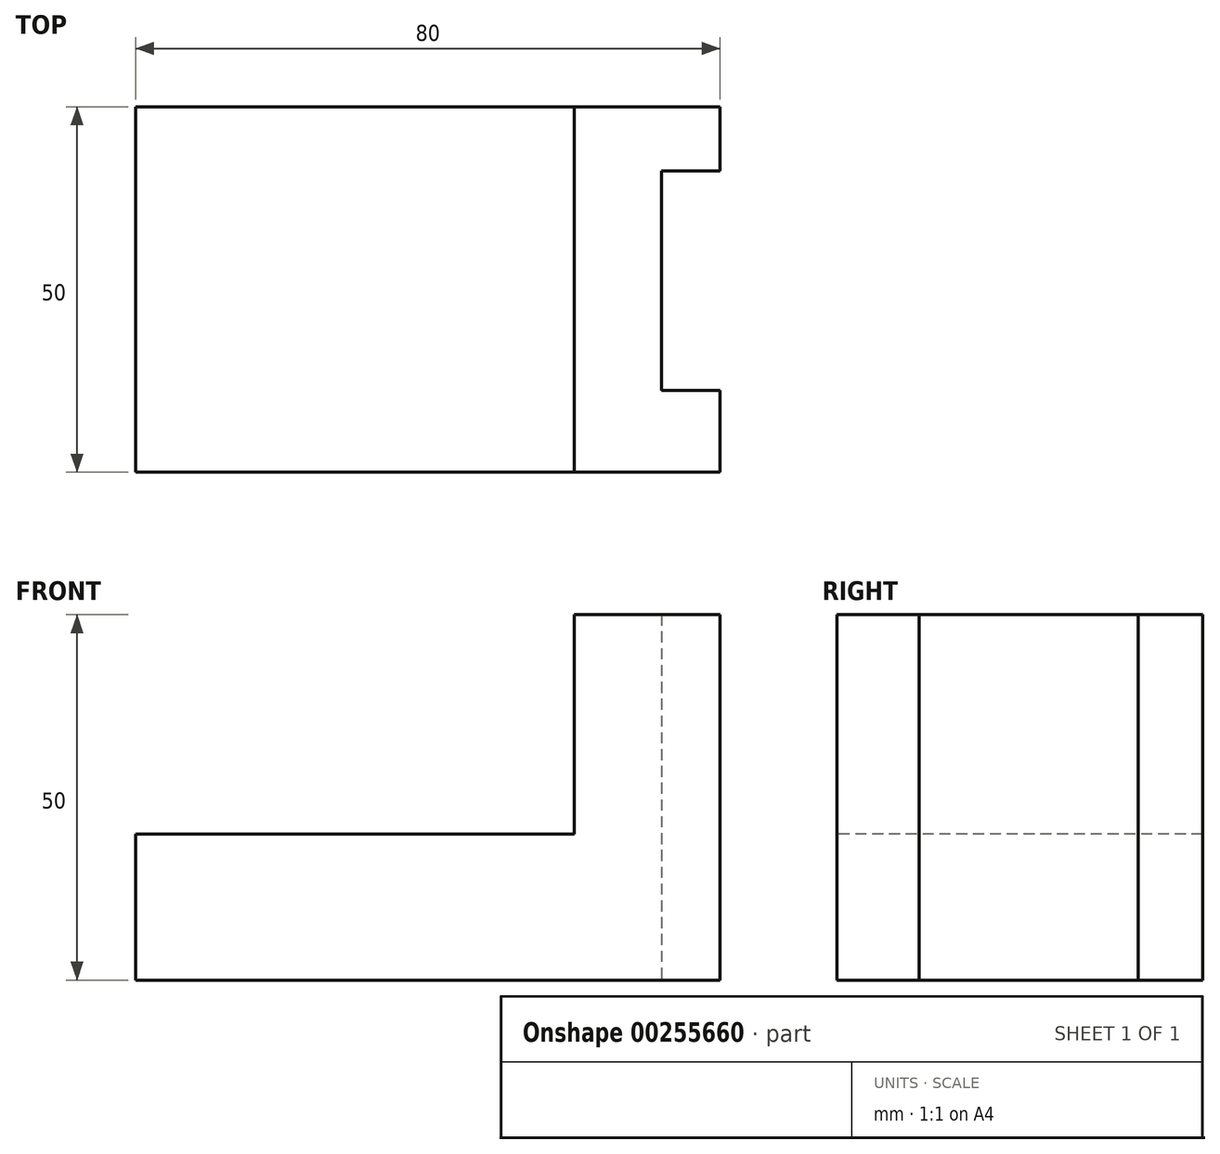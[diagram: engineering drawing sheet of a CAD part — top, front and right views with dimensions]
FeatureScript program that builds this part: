
annotation { "Feature Type Name" : "Feature", "Feature Type Description" : "" }
export const myFeature = defineFeature(function(context is Context, id is Id, definition is map)
    precondition{}
    {
        {
            var Q0;
            Q0=qCreatedBy(makeId("Top.planeOp"),FACE);
            var sketch = newSketch(context, id + "F0", { "sketchPlane" : qUnion([Q0])});
            skLineSegment(sketch, "E0.bottom", {"start": v(-136.19, 58.29) * mm, "end": v(-76.19, 58.29) * mm});
            skLineSegment(sketch, "E0.top", {"start": v(-136.19, 8.29) * mm, "end": v(-76.19, 8.29) * mm});
            skLineSegment(sketch, "E0.left", {"start": v(-136.19, 58.29) * mm, "end": v(-136.19, 8.29) * mm});
            skLineSegment(sketch, "E0.right", {"start": v(-76.19, 58.29) * mm, "end": v(-76.19, 8.29) * mm});
            skLineSegment(sketch, "E1.bottom", {"start": v(-76.19, 58.29) * mm, "end": v(-56.19, 58.29) * mm});
            skLineSegment(sketch, "E1.top", {"start": v(-76.19, 8.29) * mm, "end": v(-56.19, 8.29) * mm});
            skLineSegment(sketch, "E1.right", {"start": v(-56.19, 58.29) * mm, "end": v(-56.19, 49.5) * mm});
            skLineSegment(sketch, "E2.bottom", {"start": v(-56.19, 49.5) * mm, "end": v(-64.19, 49.5) * mm});
            skLineSegment(sketch, "E2.top", {"start": v(-56.19, 19.5) * mm, "end": v(-64.19, 19.5) * mm});
            skLineSegment(sketch, "E2.right", {"start": v(-64.19, 49.5) * mm, "end": v(-64.19, 19.5) * mm});
            skLineSegment(sketch, "E3.trimOffspring", {"start": v(-56.19, 19.5) * mm, "end": v(-56.19, 8.29) * mm});
            skSolve(sketch);
        }
        {
            var Q0;
            Q0=makeQuery(id+"F0.imprint","IMPRINT",FACE,{"disambiguationData":[TD([[makeQuery(id+"F0.imprint","IMPRINT",EDGE,{"derivedFrom":sQuery(id+"F0.wireOp",EDGE,"E1.bottom")}),-1.0]])]});
            extrude(context, id + "F1", {"entities" : qUnion([Q0]), "depth" : 50 * mm});
        }
        {
            var Q0;
            Q0=makeQuery(id+"F0.imprint","IMPRINT",FACE,{"disambiguationData":[TD([[makeQuery(id+"F0.imprint","IMPRINT",EDGE,{"derivedFrom":sQuery(id+"F0.wireOp",EDGE,"E0.bottom")}),-1.0]])]});
            extrude(context, id + "F2", {"entities" : qUnion([Q0]), "operationType" : NewBodyOperationType.ADD, "depth" : 20 * mm});
        }
    });
